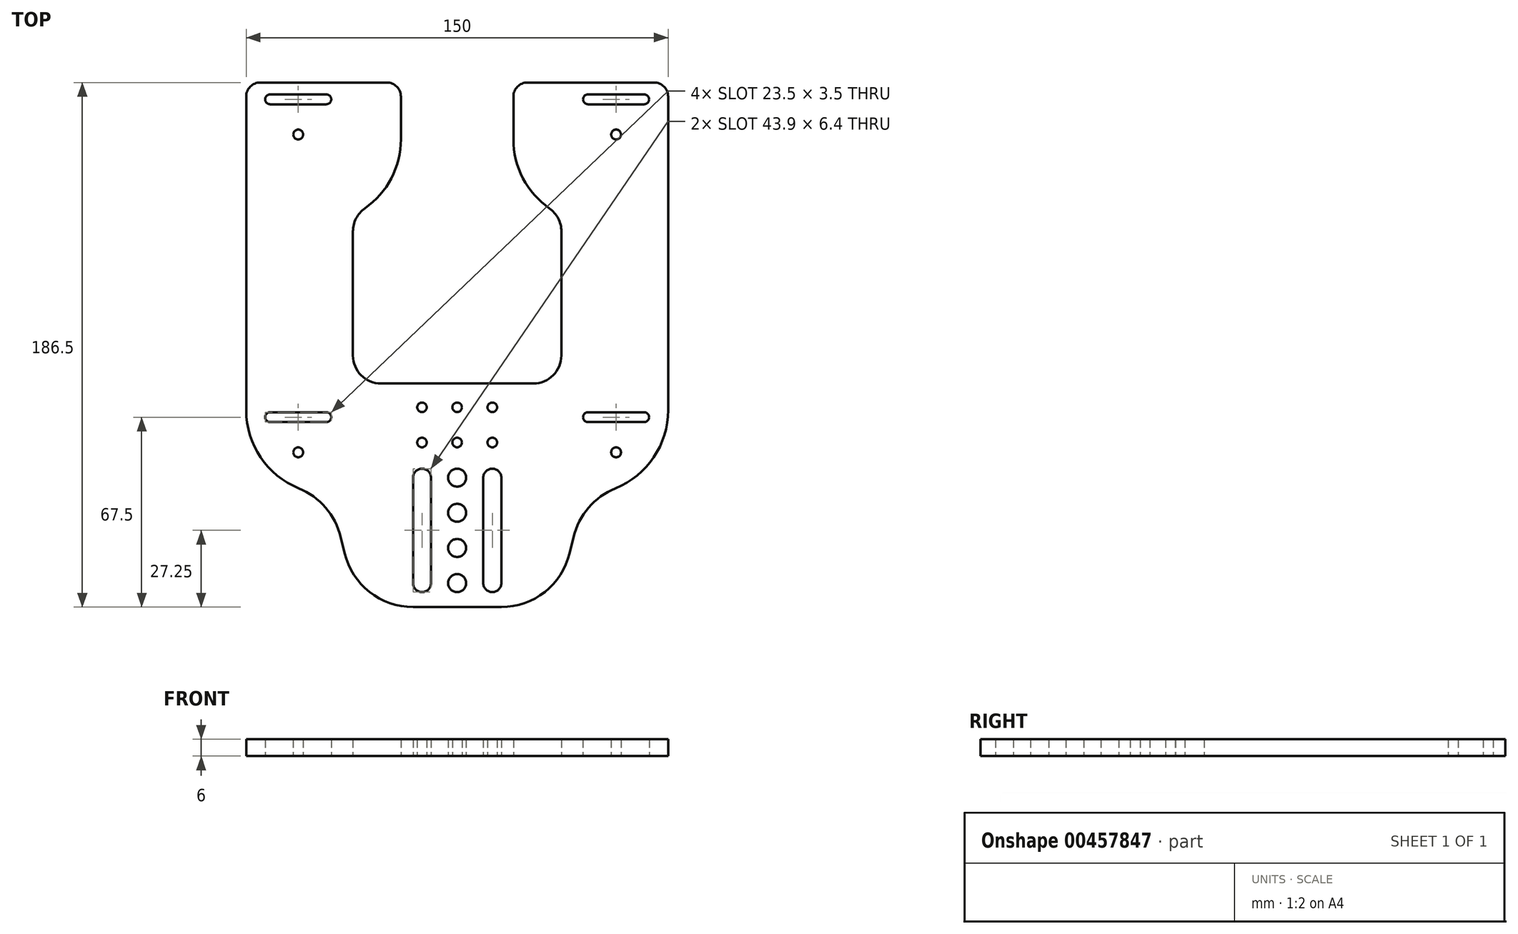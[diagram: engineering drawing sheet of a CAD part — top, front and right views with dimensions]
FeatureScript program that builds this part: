
annotation { "Feature Type Name" : "Feature", "Feature Type Description" : "" }
export const myFeature = defineFeature(function(context is Context, id is Id, definition is map)
    precondition{}
    {
        {
            var Q0;
            Q0=qCreatedBy(makeId("Top.planeOp"),FACE);
            var sketch = newSketch(context, id + "F0", { "sketchPlane" : qUnion([Q0])});
            skLineSegment(sketch, "E0.bottom", {"start": v(60, -60) * mm, "end": v(-60, -60) * mm});
            skLineSegment(sketch, "E0.top", {"start": v(60, 60) * mm, "end": v(-60, 60) * mm});
            skLineSegment(sketch, "E0.left", {"start": v(60, -60) * mm, "end": v(60, 60) * mm});
            skLineSegment(sketch, "E0.right", {"start": v(-60, -60) * mm, "end": v(-60, 60) * mm});
            skPoint(sketch, "E0.middle", {"position": v(0, 0) * mm});
            skCircle(sketch, "E1", {"center": v(-56.5, 56.5) * mm, "radius": 1.75 * mm});
            skCircle(sketch, "E2", {"center": v(56.5, 56.5) * mm, "radius": 1.75 * mm});
            skCircle(sketch, "E3", {"center": v(-56.5, -56.5) * mm, "radius": 1.75 * mm});
            skCircle(sketch, "E4", {"center": v(56.5, -56.5) * mm, "radius": 1.75 * mm});
            skCircle(sketch, "E5", {"center": v(-56.5, 56.5) * mm, "radius": 1.5 * mm, "construction": true});
            skCircle(sketch, "E6", {"center": v(-56.5, -56.5) * mm, "radius": 1.5 * mm, "construction": true});
            skCircle(sketch, "E7", {"center": v(56.5, -56.5) * mm, "radius": 1.5 * mm, "construction": true});
            skCircle(sketch, "E8", {"center": v(56.5, 56.5) * mm, "radius": 1.5 * mm, "construction": true});
            skCircle(sketch, "E9", {"center": v(-33.55, 28.55) * mm, "radius": 1.5 * mm, "construction": true});
            skCircle(sketch, "E10", {"center": v(33.55, 28.55) * mm, "radius": 1.5 * mm, "construction": true});
            skCircle(sketch, "E11", {"center": v(-33.55, -28.55) * mm, "radius": 1.5 * mm, "construction": true});
            skCircle(sketch, "E12", {"center": v(33.55, -28.55) * mm, "radius": 1.5 * mm, "construction": true});
            skLineSegment(sketch, "E13", {"start": v(-33.55, 28.55) * mm, "end": v(33.55, -28.55) * mm, "construction": true});
            skLineSegment(sketch, "E14", {"start": v(33.55, 28.55) * mm, "end": v(-33.55, -28.55) * mm, "construction": true});
            skLineSegment(sketch, "E15.bottom", {"start": v(37.05, 32.05) * mm, "end": v(-37.05, 32.05) * mm, "construction": true});
            skLineSegment(sketch, "E15.top", {"start": v(37.05, -32.05) * mm, "end": v(-37.05, -32.05) * mm, "construction": true});
            skLineSegment(sketch, "E15.left", {"start": v(37.05, 32.05) * mm, "end": v(37.05, -32.05) * mm, "construction": true});
            skLineSegment(sketch, "E15.right", {"start": v(-37.05, 32.05) * mm, "end": v(-37.05, -32.05) * mm, "construction": true});
            skLineSegment(sketch, "E16.bottom", {"start": v(15, -15) * mm, "end": v(-15, -15) * mm, "construction": true});
            skLineSegment(sketch, "E16.top", {"start": v(15, 15) * mm, "end": v(-15, 15) * mm, "construction": true});
            skLineSegment(sketch, "E16.left", {"start": v(15, -15) * mm, "end": v(15, 15) * mm, "construction": true});
            skLineSegment(sketch, "E16.right", {"start": v(-15, -15) * mm, "end": v(-15, 15) * mm, "construction": true});
            skSolve(sketch);
        }
        {
            var Q0;
            Q0=qCreatedBy(makeId("Top.planeOp"),FACE);
            var sketch = newSketch(context, id + "F1", { "sketchPlane" : qUnion([Q0])});
            skLineSegment(sketch, "E17.bottom", {"start": v(75, 75) * mm, "end": v(-75, 75) * mm});
            skLineSegment(sketch, "E17.top", {"start": v(75, -111.5) * mm, "end": v(-75, -111.5) * mm});
            skLineSegment(sketch, "E17.left", {"start": v(75, 75) * mm, "end": v(75, -111.5) * mm});
            skLineSegment(sketch, "E17.right", {"start": v(-75, 75) * mm, "end": v(-75, -111.5) * mm});
            skPoint(sketch, "E17.middle", {"position": v(0, -18.25) * mm});
            skLineSegment(sketch, "E18", {"start": v(0, 0) * mm, "end": v(0, -111.5) * mm, "construction": true});
            skCircle(sketch, "E19", {"center": v(0, -103) * mm, "radius": 3.2 * mm});
            skCircle(sketch, "E20", {"center": v(0, -90.5) * mm, "radius": 3.2 * mm});
            skCircle(sketch, "E21", {"center": v(0, -78) * mm, "radius": 3.2 * mm});
            skCircle(sketch, "E22", {"center": v(0, -65.5) * mm, "radius": 3.2 * mm});
            skArc(sketch, "E23", {"start": v(15.7, -65.5) * mm, "mid": v(12.5, -62.3) * mm, "end": v(9.3, -65.5) * mm});
            skArc(sketch, "E24", {"start": v(-9.3, -65.5) * mm, "mid": v(-12.5, -62.3) * mm, "end": v(-15.7, -65.5) * mm});
            skArc(sketch, "E25", {"start": v(-15.7, -103) * mm, "mid": v(-12.5, -106.2) * mm, "end": v(-9.3, -103) * mm});
            skArc(sketch, "E26", {"start": v(9.3, -103) * mm, "mid": v(12.5, -106.2) * mm, "end": v(15.7, -103) * mm});
            skLineSegment(sketch, "E27", {"start": v(-15.7, -65.5) * mm, "end": v(-15.7, -103) * mm});
            skLineSegment(sketch, "E28", {"start": v(-9.3, -65.5) * mm, "end": v(-9.3, -103) * mm});
            skLineSegment(sketch, "E29", {"start": v(9.3, -65.5) * mm, "end": v(9.3, -103) * mm});
            skLineSegment(sketch, "E30", {"start": v(15.7, -65.5) * mm, "end": v(15.7, -103) * mm});
            skCircle(sketch, "E31.0", {"center": v(-56.5, -56.5) * mm, "radius": 1.75 * mm});
            skCircle(sketch, "E32.0", {"center": v(56.5, -56.5) * mm, "radius": 1.75 * mm});
            skCircle(sketch, "E33.0", {"center": v(56.5, 56.5) * mm, "radius": 1.75 * mm});
            skCircle(sketch, "E34.0", {"center": v(-56.5, 56.5) * mm, "radius": 1.75 * mm});
            skArc(sketch, "E35", {"start": v(-46.5, 67.25) * mm, "mid": v(-44.75, 69) * mm, "end": v(-46.5, 70.75) * mm});
            skArc(sketch, "E36", {"start": v(-66.5, 70.75) * mm, "mid": v(-68.25, 69) * mm, "end": v(-66.5, 67.25) * mm});
            skLineSegment(sketch, "E37", {"start": v(-66.5, 70.75) * mm, "end": v(-46.5, 70.75) * mm});
            skLineSegment(sketch, "E38", {"start": v(-66.5, 67.25) * mm, "end": v(-46.5, 67.25) * mm});
            skArc(sketch, "E39", {"start": v(66.5, 67.25) * mm, "mid": v(68.25, 69) * mm, "end": v(66.5, 70.75) * mm});
            skArc(sketch, "E40", {"start": v(46.5, 70.75) * mm, "mid": v(44.75, 69) * mm, "end": v(46.5, 67.25) * mm});
            skLineSegment(sketch, "E41", {"start": v(46.5, 70.75) * mm, "end": v(66.5, 70.75) * mm});
            skLineSegment(sketch, "E42", {"start": v(46.5, 67.25) * mm, "end": v(66.5, 67.25) * mm});
            skArc(sketch, "E43", {"start": v(-46.5, -45.75) * mm, "mid": v(-44.75, -44) * mm, "end": v(-46.5, -42.25) * mm});
            skArc(sketch, "E44", {"start": v(-66.5, -42.25) * mm, "mid": v(-68.25, -44) * mm, "end": v(-66.5, -45.75) * mm});
            skLineSegment(sketch, "E45", {"start": v(-66.5, -42.25) * mm, "end": v(-46.5, -42.25) * mm});
            skLineSegment(sketch, "E46", {"start": v(-66.5, -45.75) * mm, "end": v(-46.5, -45.75) * mm});
            skArc(sketch, "E47", {"start": v(66.5, -45.75) * mm, "mid": v(68.25, -44) * mm, "end": v(66.5, -42.25) * mm});
            skArc(sketch, "E48", {"start": v(46.5, -42.25) * mm, "mid": v(44.75, -44) * mm, "end": v(46.5, -45.75) * mm});
            skLineSegment(sketch, "E49", {"start": v(46.5, -42.25) * mm, "end": v(66.5, -42.25) * mm});
            skLineSegment(sketch, "E50", {"start": v(46.5, -45.75) * mm, "end": v(66.5, -45.75) * mm});
            skCircle(sketch, "E51", {"center": v(0, -53) * mm, "radius": 1.7 * mm});
            skCircle(sketch, "E52", {"center": v(0, -40.5) * mm, "radius": 1.7 * mm});
            skCircle(sketch, "E53", {"center": v(-12.5, -40.5) * mm, "radius": 1.7 * mm});
            skPoint(sketch, "E53.centerSnap0", {"position": v(-12.5, -62.3) * mm});
            skCircle(sketch, "E54", {"center": v(12.5, -40.5) * mm, "radius": 1.7 * mm});
            skPoint(sketch, "E54.centerSnap0", {"position": v(12.5, -62.3) * mm});
            skCircle(sketch, "E55", {"center": v(12.5, -53) * mm, "radius": 1.7 * mm});
            skCircle(sketch, "E56", {"center": v(-12.5, -53) * mm, "radius": 1.7 * mm});
            skPoint(sketch, "E57.0", {"position": v(-37.05, 32.05) * mm});
            skPoint(sketch, "E58.0", {"position": v(37.05, -32.05) * mm});
            skPoint(sketch, "E59.0", {"position": v(-37.05, -32.05) * mm});
            skPoint(sketch, "E60.0", {"position": v(37.05, 32.05) * mm});
            skLineSegment(sketch, "E61.bottom", {"start": v(-37.05, 32.05) * mm, "end": v(37.05, 32.05) * mm});
            skLineSegment(sketch, "E61.top", {"start": v(-37.05, -32.05) * mm, "end": v(37.05, -32.05) * mm});
            skLineSegment(sketch, "E61.left", {"start": v(-37.05, 32.05) * mm, "end": v(-37.05, -32.05) * mm});
            skLineSegment(sketch, "E61.right", {"start": v(37.05, 32.05) * mm, "end": v(37.05, -32.05) * mm});
            skLineSegment(sketch, "E62.bottom", {"start": v(25.4, -111.5) * mm, "end": v(-25.4, -111.5) * mm, "construction": true});
            skLineSegment(sketch, "E62.top", {"start": v(25.4, -28) * mm, "end": v(-25.4, -28) * mm, "construction": true});
            skLineSegment(sketch, "E62.left", {"start": v(25.4, -111.5) * mm, "end": v(25.4, -28) * mm, "construction": true});
            skLineSegment(sketch, "E62.right", {"start": v(-25.4, -111.5) * mm, "end": v(-25.4, -28) * mm, "construction": true});
            skPoint(sketch, "E62.middle", {"position": v(0, -69.75) * mm});
            skLineSegment(sketch, "E63", {"start": v(25.4, -111.5) * mm, "end": v(35.4, -111.5) * mm});
            skLineSegment(sketch, "E64", {"start": v(35.4, -111.5) * mm, "end": v(45, -71.5) * mm});
            skLineSegment(sketch, "E65", {"start": v(45, -71.5) * mm, "end": v(75, -71.5) * mm});
            skLineSegment(sketch, "E66", {"start": v(-25.4, -111.5) * mm, "end": v(-35.4, -111.5) * mm});
            skLineSegment(sketch, "E67", {"start": v(-35.4, -111.5) * mm, "end": v(-45, -71.5) * mm});
            skLineSegment(sketch, "E68", {"start": v(-45, -71.5) * mm, "end": v(-75, -71.5) * mm});
            skLineSegment(sketch, "E69.bottom", {"start": v(-20, 75) * mm, "end": v(20, 75) * mm});
            skLineSegment(sketch, "E69.top", {"start": v(-20, 32.05) * mm, "end": v(20, 32.05) * mm});
            skLineSegment(sketch, "E69.left", {"start": v(-20, 75) * mm, "end": v(-20, 32.05) * mm});
            skLineSegment(sketch, "E69.right", {"start": v(20, 75) * mm, "end": v(20, 32.05) * mm});
            skSolve(sketch);
        }
        {
            var Q0;
            Q0=makeQuery(id+"F1.imprint","IMPRINT",FACE,{"disambiguationData":[TD([[makeQuery(id+"F1.imprint","IMPRINT",EDGE,{"derivedFrom":sQuery(id+"F1.wireOp",EDGE,"E19")}),-1.0]])]});
            extrude(context, id + "F2", {"entities" : qUnion([Q0]), "depth" : 6 * mm});
        }
        {
            var Q0;
            Q0=makeQuery(id+"F2.opExtrude","SWEPT_EDGE",EDGE,{"disambiguationData":[OSD([sQuery(id+"F1.wireOp",EDGE,"E17.top"),sQuery(id+"F1.wireOp",EDGE,"E63"),sQuery(id+"F1.wireOp",EDGE,"E64")])]});
            var Q1;
            Q1=makeQuery(id+"F2.opExtrude","SWEPT_EDGE",EDGE,{"disambiguationData":[OSD([sQuery(id+"F1.wireOp",EDGE,"E17.top"),sQuery(id+"F1.wireOp",EDGE,"E66"),sQuery(id+"F1.wireOp",EDGE,"E67")])]});
            fillet(context, id + "F3", {"entities" : qUnion([Q0, Q1]), "radius" : 25 * mm, "tangentPropagation" : true, "allowEdgeOverflow" : false});
        }
        {
            var Q0;
            Q0=makeQuery(id+"F2.opExtrude","SWEPT_EDGE",EDGE,{"disambiguationData":[OSD([sQuery(id+"F1.wireOp",EDGE,"E17.left"),sQuery(id+"F1.wireOp",EDGE,"E65")])]});
            var Q1;
            Q1=makeQuery(id+"F2.opExtrude","SWEPT_EDGE",EDGE,{"disambiguationData":[OSD([sQuery(id+"F1.wireOp",EDGE,"E17.right"),sQuery(id+"F1.wireOp",EDGE,"E68")])]});
            fillet(context, id + "F4", {"entities" : qUnion([Q0, Q1]), "radius" : 30 * mm, "tangentPropagation" : true, "allowEdgeOverflow" : false});
        }
        {
            var Q0;
            Q0=makeQuery(id+"F2.opExtrude","SWEPT_EDGE",EDGE,{"disambiguationData":[OSD([sQuery(id+"F1.wireOp",EDGE,"E61.top"),sQuery(id+"F1.wireOp",EDGE,"E61.left")])]});
            var Q1;
            Q1=makeQuery(id+"F2.opExtrude","SWEPT_EDGE",EDGE,{"disambiguationData":[OSD([sQuery(id+"F1.wireOp",EDGE,"E61.top"),sQuery(id+"F1.wireOp",EDGE,"E61.right")])]});
            var Q2;
            Q2=makeQuery(id+"F2.opExtrude","SWEPT_EDGE",EDGE,{"disambiguationData":[OSD([sQuery(id+"F1.wireOp",EDGE,"E61.bottom"),sQuery(id+"F1.wireOp",EDGE,"E61.right")])]});
            var Q3;
            Q3=makeQuery(id+"F2.opExtrude","SWEPT_EDGE",EDGE,{"disambiguationData":[OSD([sQuery(id+"F1.wireOp",EDGE,"E61.bottom"),sQuery(id+"F1.wireOp",EDGE,"E61.left")])]});
            fillet(context, id + "F5", {"entities" : qUnion([Q0, Q1, Q2, Q3]), "radius" : 10 * mm, "tangentPropagation" : true, "allowEdgeOverflow" : false});
        }
        {
            var Q0;
            Q0=makeQuery(id+"F2.opExtrude","SWEPT_EDGE",EDGE,{"disambiguationData":[OSD([sQuery(id+"F1.wireOp",EDGE,"E61.bottom"),sQuery(id+"F1.wireOp",EDGE,"E69.top"),sQuery(id+"F1.wireOp",EDGE,"E69.left")])]});
            var Q1;
            Q1=makeQuery(id+"F2.opExtrude","SWEPT_EDGE",EDGE,{"disambiguationData":[OSD([sQuery(id+"F1.wireOp",EDGE,"E61.bottom"),sQuery(id+"F1.wireOp",EDGE,"E69.top"),sQuery(id+"F1.wireOp",EDGE,"E69.right")])]});
            fillet(context, id + "F6", {"entities" : qUnion([Q0, Q1]), "radius" : 30 * mm, "tangentPropagation" : true, "allowEdgeOverflow" : false});
        }
        {
            var Q0;
            Q0=makeQuery(id+"F2.opExtrude","SWEPT_EDGE",EDGE,{"disambiguationData":[OSD([sQuery(id+"F1.wireOp",EDGE,"E17.bottom"),sQuery(id+"F1.wireOp",EDGE,"E17.right")])]});
            var Q1;
            Q1=makeQuery(id+"F2.opExtrude","SWEPT_EDGE",EDGE,{"disambiguationData":[OSD([sQuery(id+"F1.wireOp",EDGE,"E17.bottom"),sQuery(id+"F1.wireOp",EDGE,"E17.left")])]});
            var Q2;
            Q2=makeQuery(id+"F2.opExtrude","SWEPT_EDGE",EDGE,{"disambiguationData":[OSD([sQuery(id+"F1.wireOp",EDGE,"E17.bottom"),sQuery(id+"F1.wireOp",EDGE,"E69.bottom"),sQuery(id+"F1.wireOp",EDGE,"E69.left")])]});
            var Q3;
            Q3=makeQuery(id+"F2.opExtrude","SWEPT_EDGE",EDGE,{"disambiguationData":[OSD([sQuery(id+"F1.wireOp",EDGE,"E17.bottom"),sQuery(id+"F1.wireOp",EDGE,"E69.bottom"),sQuery(id+"F1.wireOp",EDGE,"E69.right")])]});
            fillet(context, id + "F7", {"entities" : qUnion([Q0, Q1, Q2, Q3]), "radius" : 5 * mm, "tangentPropagation" : true, "allowEdgeOverflow" : false});
        }
        {
            var Q0;
            Q0=makeQuery(id+"F4.opFillet","BLEND_EDGE",EDGE,{"blendedFrom":[makeQuery(id+"F2.opExtrude","SWEPT_EDGE",EDGE,{"disambiguationData":[OSD([sQuery(id+"F1.wireOp",EDGE,"E17.left"),sQuery(id+"F1.wireOp",EDGE,"E65")])]}),makeQuery(id+"F2.opExtrude","SWEPT_FACE",FACE,{"disambiguationData":[OSD([sQuery(id+"F1.wireOp",EDGE,"E64")])]})],"blendedInto":[makeQuery(id+"F2.opExtrude","SWEPT_FACE",FACE,{"disambiguationData":[OSD([sQuery(id+"F1.wireOp",EDGE,"E64")])]})]});
            var Q1;
            Q1=makeQuery(id+"F4.opFillet","BLEND_EDGE",EDGE,{"blendedFrom":[makeQuery(id+"F2.opExtrude","SWEPT_EDGE",EDGE,{"disambiguationData":[OSD([sQuery(id+"F1.wireOp",EDGE,"E17.right"),sQuery(id+"F1.wireOp",EDGE,"E68")])]}),makeQuery(id+"F2.opExtrude","SWEPT_FACE",FACE,{"disambiguationData":[OSD([sQuery(id+"F1.wireOp",EDGE,"E67")])]})],"blendedInto":[makeQuery(id+"F2.opExtrude","SWEPT_FACE",FACE,{"disambiguationData":[OSD([sQuery(id+"F1.wireOp",EDGE,"E67")])]})]});
            fillet(context, id + "F8", {"entities" : qUnion([Q0, Q1]), "radius" : 25 * mm, "tangentPropagation" : true, "allowEdgeOverflow" : false});
        }
    });
